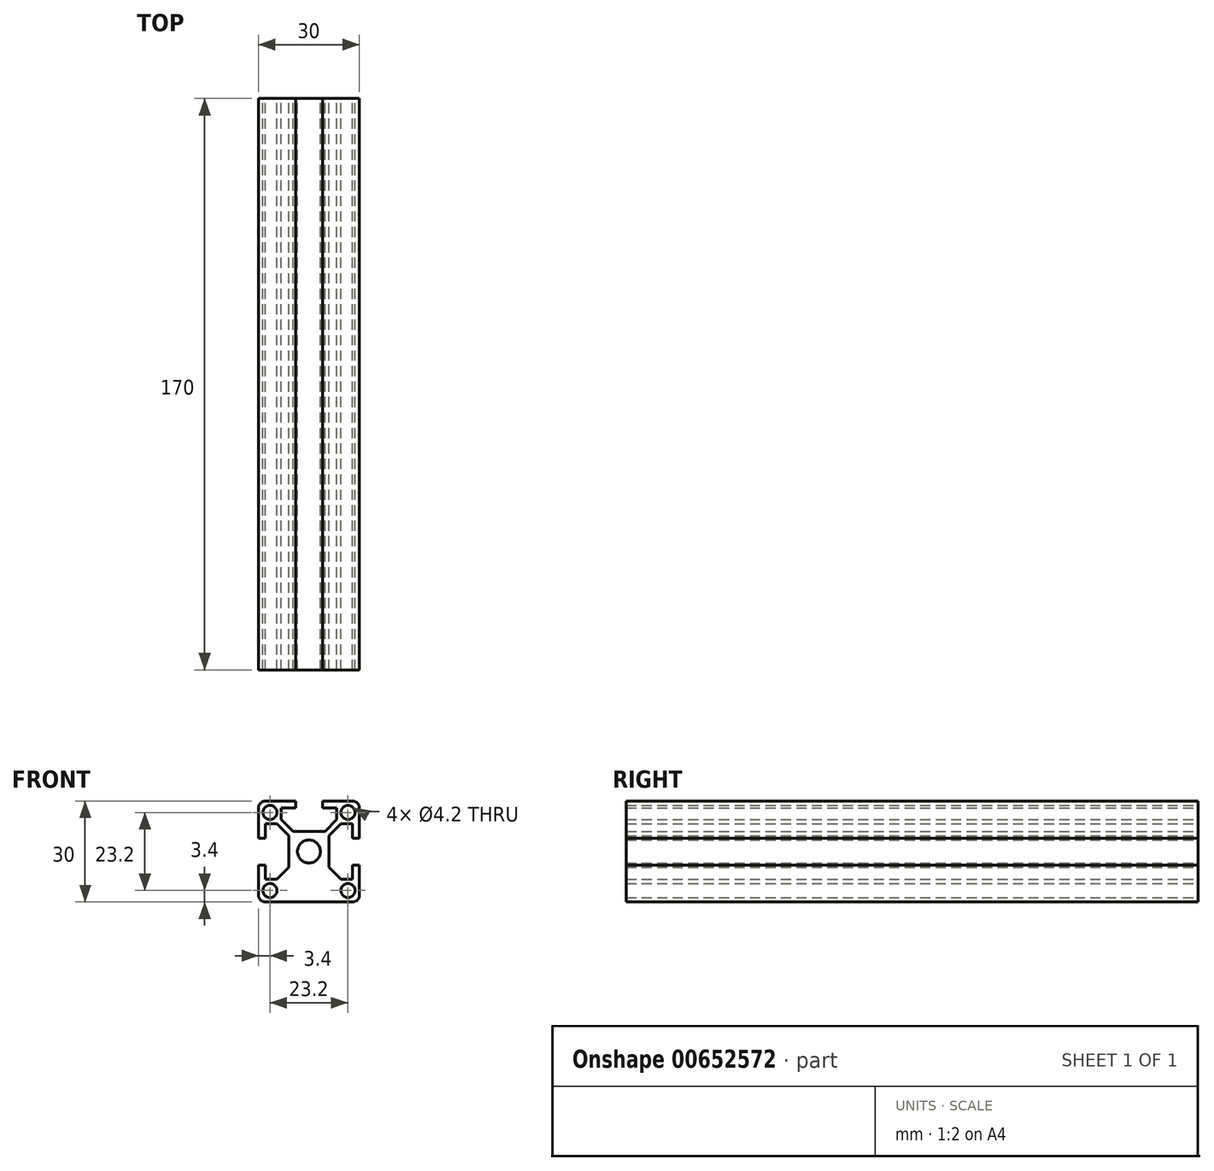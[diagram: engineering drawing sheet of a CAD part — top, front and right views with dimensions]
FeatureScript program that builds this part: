
annotation { "Feature Type Name" : "Feature", "Feature Type Description" : "" }
export const myFeature = defineFeature(function(context is Context, id is Id, definition is map)
    precondition{}
    {
        {
            var Q0;
            Q0=qCreatedBy(makeId("Front.planeOp"),FACE);
            var sketch = newSketch(context, id + "F0", { "sketchPlane" : qUnion([Q0])});
            skLineSegment(sketch, "E0.bottom", {"start": v(15, 15) * mm, "end": v(-15, 15) * mm});
            skLineSegment(sketch, "E0.top", {"start": v(15, -15) * mm, "end": v(-15, -15) * mm});
            skLineSegment(sketch, "E0.left", {"start": v(15, 15) * mm, "end": v(15, -15) * mm});
            skLineSegment(sketch, "E0.right", {"start": v(-15, 15) * mm, "end": v(-15, -15) * mm});
            skPoint(sketch, "E0.middle", {"position": v(0, 0) * mm});
            skLineSegment(sketch, "E1", {"start": v(-4, 15) * mm, "end": v(-4, 13) * mm});
            skLineSegment(sketch, "E2", {"start": v(-4, 13) * mm, "end": v(-8.25, 13) * mm});
            skLineSegment(sketch, "E3", {"start": v(-8.25, 13) * mm, "end": v(-8.25, 9.5) * mm});
            skLineSegment(sketch, "E4", {"start": v(-8.25, 9.5) * mm, "end": v(-4.75, 6) * mm});
            skLineSegment(sketch, "E5", {"start": v(-4.75, 6) * mm, "end": v(4.75, 6) * mm});
            skLineSegment(sketch, "E6", {"start": v(4.75, 6) * mm, "end": v(8.25, 9.5) * mm});
            skLineSegment(sketch, "E7", {"start": v(8.25, 9.5) * mm, "end": v(8.25, 13) * mm});
            skLineSegment(sketch, "E8", {"start": v(8.25, 13) * mm, "end": v(4, 13) * mm});
            skLineSegment(sketch, "E9", {"start": v(4, 13) * mm, "end": v(4, 15) * mm});
            skSolve(sketch);
        }
        {
            var Q0;
            Q0=makeQuery(id+"F0.imprint","IMPRINT",FACE,{"disambiguationData":[TD([[makeQuery(id+"F0.imprint","IMPRINT",EDGE,{"derivedFrom":sQuery(id+"F0.wireOp",EDGE,"E0.top")}),-1.0]])]});
            var Q1;
            {var subQ0=sQuery(id+"F0.wireOp",EDGE,"E1");Q1=makeQuery(id+"F0.imprint","IMPRINT",FACE,{"disambiguationData":[TD([[makeQuery(id+"F0.imprint","IMPRINT",EDGE,{"derivedFrom":subQ0}),1.0]])]});}
            extrude(context, id + "F1", {"entities" : qUnion([Q0, Q1]), "depth" : 170 * mm, "offsetDistance" : 25 * mm});
        }
        {
            var Q0;
            {var subQ0=sQuery(id+"F0.wireOp",EDGE,"E1");Q0=makeQuery(id+"F0.imprint","IMPRINT",FACE,{"disambiguationData":[TD([[makeQuery(id+"F0.imprint","IMPRINT",EDGE,{"derivedFrom":subQ0}),1.0]])]});}
            extrude(context, id + "F2", {"entities" : qUnion([Q0]), "operationType" : NewBodyOperationType.REMOVE, "depth" : 400 * mm, "offsetDistance" : 25 * mm});
        }
        {
            var Q0;
            Q0=makeQuery(id+"F1.opExtrude","CAP_FACE",FACE,{"disambiguationData":[OSD([sQuery(id+"F0.wireOp",EDGE,"E0.bottom"),sQuery(id+"F0.wireOp",EDGE,"E0.top"),sQuery(id+"F0.wireOp",EDGE,"E0.left"),sQuery(id+"F0.wireOp",EDGE,"E0.right")])],"isStart":true});
            var sketch = newSketch(context, id + "F3", { "sketchPlane" : qUnion([Q0])});
            skLineSegment(sketch, "E10.bottom", {"start": v(-9.5, 8.25) * mm, "end": v(-13, 8.25) * mm});
            skLineSegment(sketch, "E10.top", {"start": v(-9.5, -8.25) * mm, "end": v(-13, -8.25) * mm});
            skLineSegment(sketch, "E10.left", {"start": v(-6, 4.75) * mm, "end": v(-6, -4.75) * mm});
            skLineSegment(sketch, "E10.right", {"start": v(-13, 8.25) * mm, "end": v(-13, -8.25) * mm});
            skLineSegment(sketch, "E11.bottom", {"start": v(-13, 4) * mm, "end": v(-31.65, 4) * mm});
            skLineSegment(sketch, "E11.top", {"start": v(-13, -4) * mm, "end": v(-31.65, -4) * mm});
            skLineSegment(sketch, "E11.left", {"start": v(-13, 4) * mm, "end": v(-13, -4) * mm});
            skLineSegment(sketch, "E11.right", {"start": v(-31.65, 4) * mm, "end": v(-31.65, -4) * mm});
            skLineSegment(sketch, "E12.bottom", {"start": v(9.5, 8.25) * mm, "end": v(13, 8.25) * mm});
            skLineSegment(sketch, "E12.top", {"start": v(9.5, -8.25) * mm, "end": v(13, -8.25) * mm});
            skLineSegment(sketch, "E12.left", {"start": v(6, 4.75) * mm, "end": v(6, -4.75) * mm});
            skLineSegment(sketch, "E12.right", {"start": v(13, 8.25) * mm, "end": v(13, -8.25) * mm});
            skLineSegment(sketch, "E13.bottom", {"start": v(13, 4) * mm, "end": v(32.96, 4) * mm});
            skLineSegment(sketch, "E13.top", {"start": v(13, -4) * mm, "end": v(32.96, -4) * mm});
            skLineSegment(sketch, "E13.left", {"start": v(13, 4) * mm, "end": v(13, -4) * mm});
            skLineSegment(sketch, "E13.right", {"start": v(32.96, 4) * mm, "end": v(32.96, -4) * mm});
            skCircle(sketch, "E14", {"center": v(0, 0) * mm, "radius": 3.4 * mm});
            skCircle(sketch, "E15", {"center": v(-11.6, 11.6) * mm, "radius": 2.1 * mm});
            skCircle(sketch, "E16", {"center": v(-11.6, -11.6) * mm, "radius": 2.1 * mm});
            skCircle(sketch, "E17", {"center": v(11.6, -11.6) * mm, "radius": 2.1 * mm});
            skCircle(sketch, "E18", {"center": v(11.6, 11.6) * mm, "radius": 2.1 * mm});
            skLineSegment(sketch, "E19", {"start": v(-9.5, 8.25) * mm, "end": v(-6, 4.75) * mm});
            skLineSegment(sketch, "E20", {"start": v(-9.5, -8.25) * mm, "end": v(-6, -4.75) * mm});
            skPoint(sketch, "E21.orphan", {"position": v(-6, 8.25) * mm});
            skPoint(sketch, "E22.orphan", {"position": v(-6, -8.25) * mm});
            skLineSegment(sketch, "E23", {"start": v(9.5, 8.25) * mm, "end": v(6, 4.75) * mm});
            skLineSegment(sketch, "E24", {"start": v(9.5, -8.25) * mm, "end": v(6, -4.75) * mm});
            skPoint(sketch, "E25.orphan", {"position": v(6, 8.25) * mm});
            skPoint(sketch, "E26.orphan", {"position": v(6, -8.25) * mm});
            skSolve(sketch);
        }
        {
            var Q0;
            Q0=qSketchRegion(id+"F3",true);
            extrude(context, id + "F4", {"entities" : qUnion([Q0]), "operationType" : NewBodyOperationType.REMOVE, "oppositeDirection" : true, "depth" : 170 * mm, "offsetDistance" : 25 * mm});
        }
        {
            var Q0;
            Q0=makeQuery(id+"F1.opExtrude","SWEPT_EDGE",EDGE,{"disambiguationData":[OSD([sQuery(id+"F0.wireOp",EDGE,"E0.bottom"),sQuery(id+"F0.wireOp",EDGE,"E0.right")])]});
            var Q1;
            Q1=makeQuery(id+"F1.opExtrude","SWEPT_EDGE",EDGE,{"disambiguationData":[OSD([sQuery(id+"F0.wireOp",EDGE,"E0.top"),sQuery(id+"F0.wireOp",EDGE,"E0.right")])]});
            var Q2;
            Q2=makeQuery(id+"F1.opExtrude","SWEPT_EDGE",EDGE,{"disambiguationData":[OSD([sQuery(id+"F0.wireOp",EDGE,"E0.top"),sQuery(id+"F0.wireOp",EDGE,"E0.left")])]});
            var Q3;
            Q3=makeQuery(id+"F1.opExtrude","SWEPT_EDGE",EDGE,{"disambiguationData":[OSD([sQuery(id+"F0.wireOp",EDGE,"E0.bottom"),sQuery(id+"F0.wireOp",EDGE,"E0.left")])]});
            fillet(context, id + "F5", {"entities" : qUnion([Q0, Q1, Q2, Q3]), "radius" : 2 * mm, "tangentPropagation" : true, "allowEdgeOverflow" : false});
        }
    });
